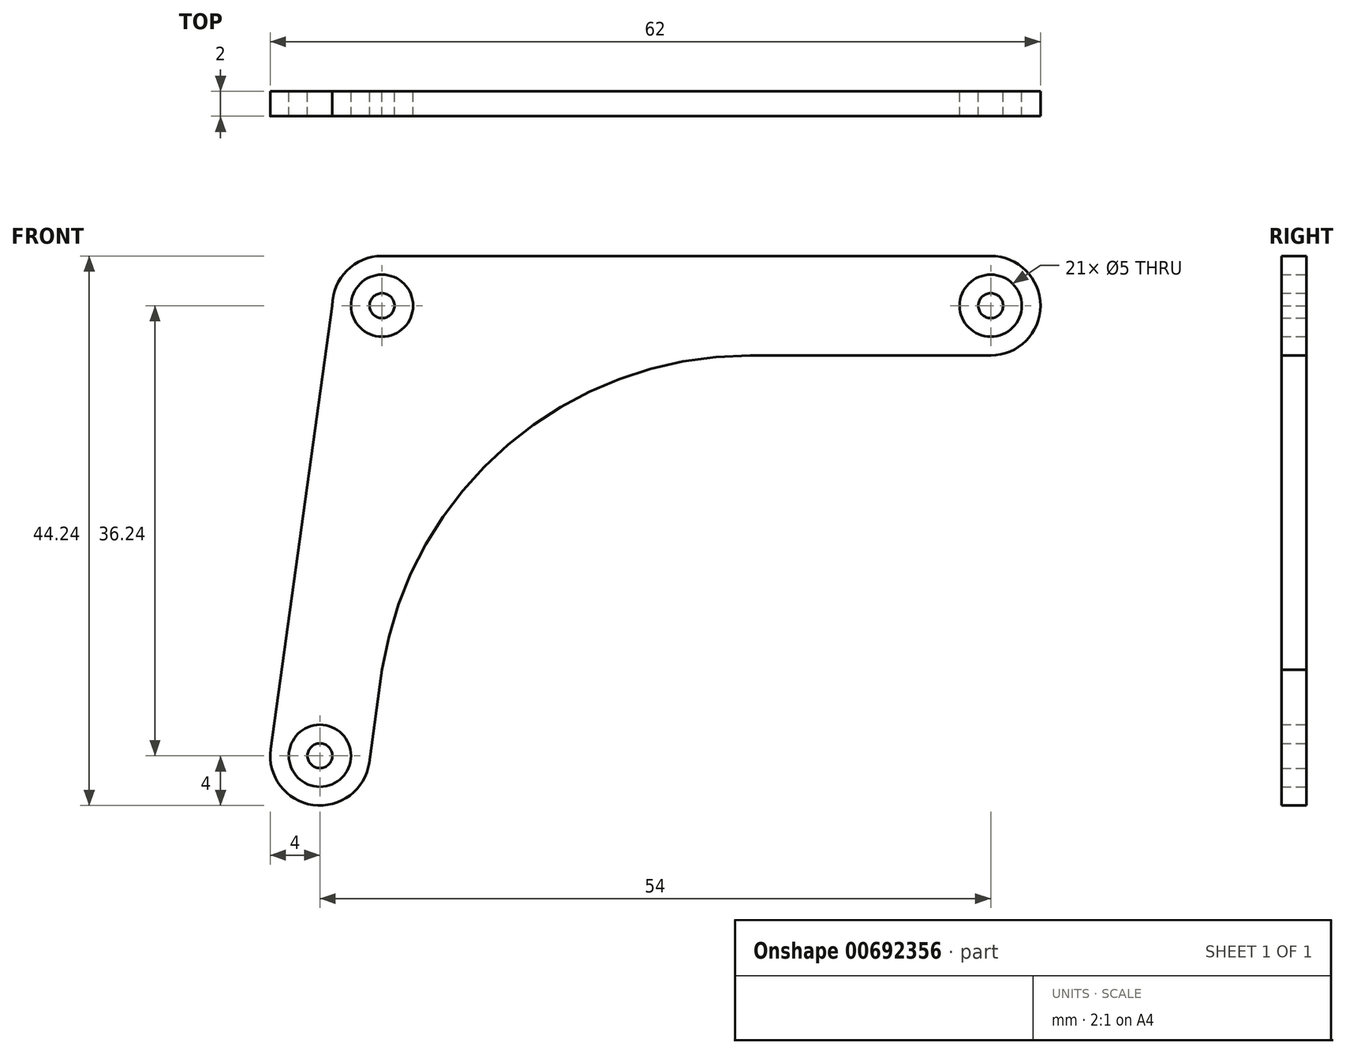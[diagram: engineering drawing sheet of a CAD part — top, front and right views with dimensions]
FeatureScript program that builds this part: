
annotation { "Feature Type Name" : "Feature", "Feature Type Description" : "" }
export const myFeature = defineFeature(function(context is Context, id is Id, definition is map)
    precondition{}
    {
        {
            var Q0;
            Q0=qCreatedBy(makeId("Front.planeOp"),FACE);
            var sketch = newSketch(context, id + "F0", { "sketchPlane" : qUnion([Q0])});
            skCircle(sketch, "E0", {"center": v(0, 0) * mm, "radius": 2.5 * mm});
            skCircle(sketch, "E1", {"center": v(0, 0) * mm, "radius": 4 * mm});
            skArc(sketch, "E2", {"start": v(-8.96, -35.69) * mm, "mid": v(-5.55, -40.2) * mm, "end": v(-1.04, -36.8) * mm});
            skArc(sketch, "E3", {"start": v(49, -4) * mm, "mid": v(53, 0) * mm, "end": v(49, 4) * mm});
            skLineSegment(sketch, "E4", {"start": v(0, 4) * mm, "end": v(49, 4) * mm});
            skArc(sketch, "E5", {"start": v(29.63, -4) * mm, "mid": v(10.14, -11.2) * mm, "end": v(0, -29.32) * mm});
            skLineSegment(sketch, "E6", {"start": v(49, -4) * mm, "end": v(29.63, -4) * mm});
            skLineSegment(sketch, "E7", {"start": v(-4, 0) * mm, "end": v(-8.96, -35.69) * mm});
            skLineSegment(sketch, "E8.trimOffspring", {"start": v(0, -29.32) * mm, "end": v(-1.04, -36.8) * mm});
            skPoint(sketch, "E9.start.orphan", {"position": v(4, 0) * mm});
            skCircle(sketch, "E10", {"center": v(-5, -36.24) * mm, "radius": 2.5 * mm});
            skCircle(sketch, "E11", {"center": v(49, 0) * mm, "radius": 2.5 * mm});
            skSolve(sketch);
        }
        {
            var Q0;
            Q0 = qSketchRegion(id + "F0", true);
            extrude(context, id + "F1", {"entities" : qUnion([Q0]), "depth" : 2 * mm, "offsetDistance" : 25 * mm});
        }
        {
            var Q0;
            Q0=qCreatedBy(makeId("Front.planeOp"),FACE);
            var sketch = newSketch(context, id + "F2", { "sketchPlane" : qUnion([Q0])});
            skCircle(sketch, "E12", {"center": v(0, 0) * mm, "radius": 1 * mm});
            skCircle(sketch, "E13", {"center": v(49, 0) * mm, "radius": 1 * mm});
            skCircle(sketch, "E14", {"center": v(-5, -36.24) * mm, "radius": 1 * mm});
            skSolve(sketch);
        }
        {
            var Q0;
            Q0 = qSketchRegion(id + "F2", true);
            extrude(context, id + "F3", {"entities" : qUnion([Q0]), "depth" : 2 * mm, "offsetDistance" : 25 * mm});
        }
    });
